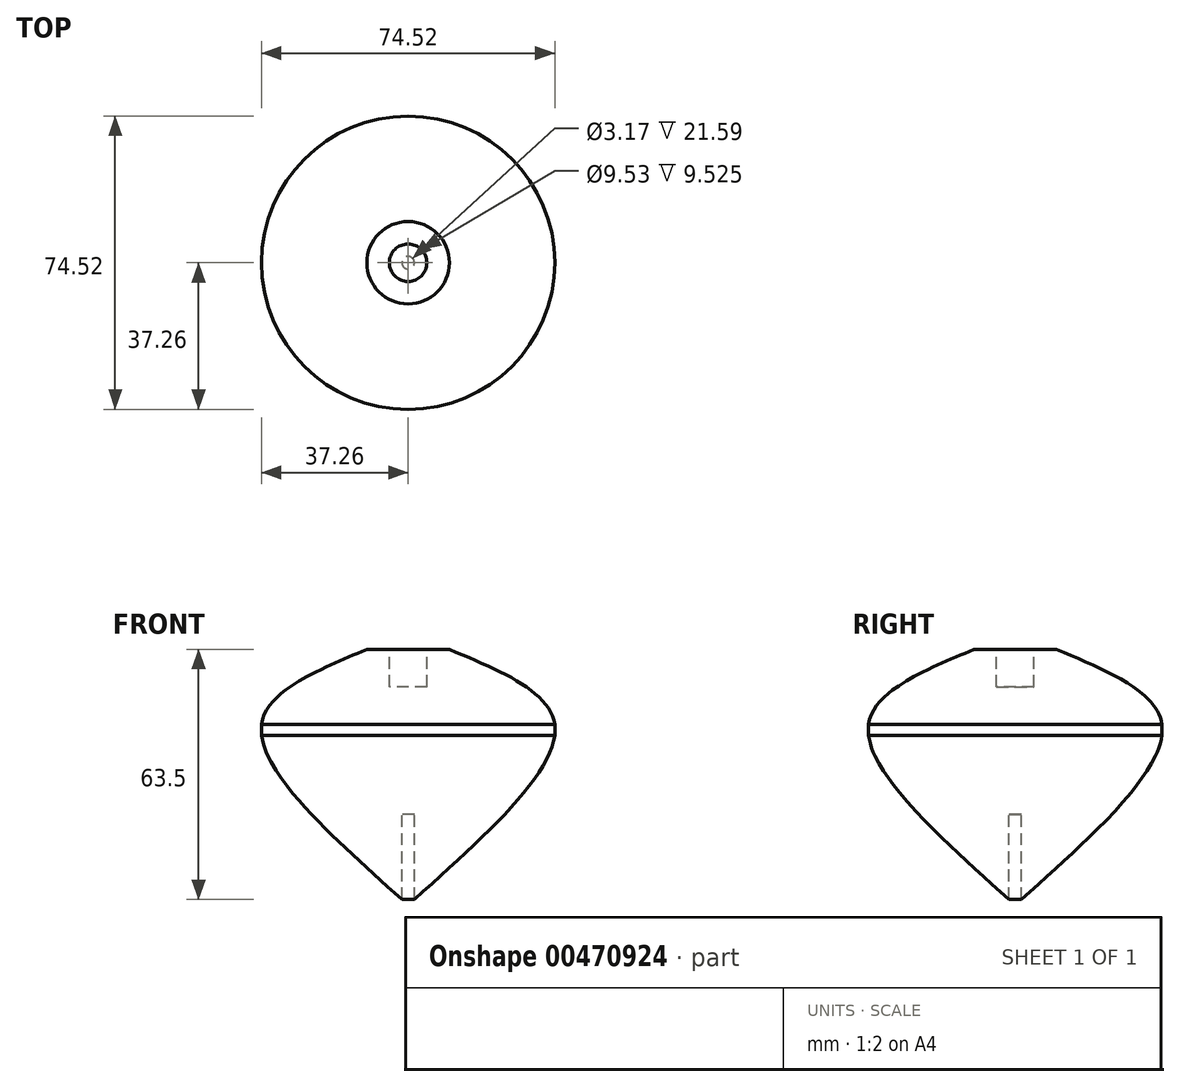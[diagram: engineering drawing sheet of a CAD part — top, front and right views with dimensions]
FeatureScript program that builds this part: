
annotation { "Feature Type Name" : "Feature", "Feature Type Description" : "" }
export const myFeature = defineFeature(function(context is Context, id is Id, definition is map)
    precondition{}
    {
        {
            var Q0;
            Q0=qCreatedBy(makeId("Front.planeOp"),FACE);
            var sketch = newSketch(context, id + "F0", { "sketchPlane" : qUnion([Q0])});
            skLineSegment(sketch, "E0.bottom", {"start": v(37.26, 31.75) * mm, "end": v(-37.26, 31.75) * mm});
            skLineSegment(sketch, "E0.top", {"start": v(37.26, -31.75) * mm, "end": v(-37.26, -31.75) * mm});
            skLineSegment(sketch, "E0.left", {"start": v(37.26, 31.75) * mm, "end": v(37.26, -31.75) * mm});
            skLineSegment(sketch, "E0.right", {"start": v(-37.26, 31.75) * mm, "end": v(-37.26, -31.75) * mm});
            skPoint(sketch, "E0.middle", {"position": v(0, 0) * mm});
            skLineSegment(sketch, "E1.bottom", {"start": v(-1.59, -31.75) * mm, "end": v(1.59, -31.75) * mm});
            skLineSegment(sketch, "E1.top", {"start": v(-1.59, -10.16) * mm, "end": v(1.59, -10.16) * mm});
            skLineSegment(sketch, "E1.left", {"start": v(-1.59, -31.75) * mm, "end": v(-1.59, -10.16) * mm});
            skLineSegment(sketch, "E1.right", {"start": v(1.59, -31.75) * mm, "end": v(1.59, -10.16) * mm});
            skPoint(sketch, "E1.middle", {"position": v(0, -20.96) * mm});
            skLineSegment(sketch, "E2.bottom", {"start": v(-4.76, 31.75) * mm, "end": v(4.76, 31.75) * mm});
            skLineSegment(sketch, "E2.top", {"start": v(-4.76, 22.23) * mm, "end": v(4.76, 22.23) * mm});
            skLineSegment(sketch, "E2.left", {"start": v(-4.76, 31.75) * mm, "end": v(-4.76, 22.23) * mm});
            skLineSegment(sketch, "E2.right", {"start": v(4.76, 31.75) * mm, "end": v(4.76, 22.23) * mm});
            skPoint(sketch, "E2.middle", {"position": v(0, 26.99) * mm});
            skPoint(sketch, "E2.middle.positionSnap0", {"position": v(0, 31.75) * mm});
            skPoint(sketch, "E2.centerSnap0", {"position": v(0, 31.75) * mm});
            skLineSegment(sketch, "E3", {"start": v(-4.76, 31.75) * mm, "end": v(-10.48, 31.75) * mm});
            skLineSegment(sketch, "E4", {"start": v(4.76, 31.75) * mm, "end": v(10.48, 31.75) * mm});
            skLineSegment(sketch, "E5", {"start": v(37.26, 31.75) * mm, "end": v(37.26, 12.7) * mm});
            skFitSpline(sketch, "E6", {"points": [v(10.48, 31.75) * mm, v(37.26, 12.7) * mm, v(1.59, -31.75) * mm], "startDerivative": vector(88.98, -36.78) * mm, "endDerivative": vector(-98.22, -87.89) * mm});
            skLineSegment(sketch, "E7", {"start": v(-37.26, 31.75) * mm, "end": v(-37.26, 12.7) * mm});
            skFitSpline(sketch, "E8", {"points": [v(-10.48, 31.75) * mm, v(-37.26, 12.7) * mm, v(-1.59, -31.75) * mm], "startDerivative": vector(-88.98, -36.78) * mm, "endDerivative": vector(98.22, -87.89) * mm});
            skLineSegment(sketch, "E9", {"start": v(0, 31.75) * mm, "end": v(0, -31.75) * mm});
            skSolve(sketch);
        }
        {
            var Q0;
            {var subQ0=sQuery(id+"F0.wireOp",EDGE,"E1.left");Q0=makeQuery(id+"F0.imprint","IMPRINT",FACE,{"disambiguationData":[TD([[makeQuery(id+"F0.imprint","IMPRINT",EDGE,{"derivedFrom":subQ0}),1.0]])]});}
            var Q1;
            Q1=sQuery(id+"F0.wireOp",EDGE,"E9");
            revolve(context, id + "F1", {"entities" : qUnion([Q0]), "axis" : qUnion([Q1]), "revolveType" : RevolveType.FULL});
        }
    });
